# Revit family: Faucet-Wall_Mount_Utility-KALLISTA-Kallista_Foundations-P31570
name_source: partatom
category: Plumbing Fixtures
units: mm (PartAtom-declared; Revit-internal decimal feet)

## family parameters
Cut with Voids When Loaded = No
Host = Face
OmniClass Number = 23.31.11.00
Part Type = Normal
Room Calculation Point = No
Round Connector Dimension = Use Diameter
Shared = No

## types (6) — shared parameters
ADA Compliant = No
Assembly Code = D2010
CW Connection = Yes
Cold Water Inlet = Cold Water Inlet
Date Modified = 03/06/2024
Default Elevation = 36"
Description = Traditional Wall Mount Pot Filler
Drain Included = No
Flow Rate = 3 GPM
HW Connection = Yes
Handle Clearance 1 = 2 5/16"
Handle Clearance 2 = 2 5/16"
Height = 5 1/4"
Hot Water Inlet = Hot Water Inlet
L1 = 13 1/8"
L2 = 8 7/8"
Length = 22"
Manufacturer = Kallista Co.
Master Format 2014 = 22 41 39
Master Format 2014 Name = Residential Faucets, Supplies, and Trim
Material = Premium Metal Construction
Pressure = 60.00 psi
Product Name = Kallista Foundations
Spout Reach = 4 1/4"
URL = https://www.kallista.com
Vent Connection = No
Waste Connection = No
Waste Water Outlet = Waste Water Outlet
WaterSense Certified = No
Width = 2 3/4"

## per-type parameters (varying)
| type | Finish | Model | Type |
| AD-Nickel Silver | Kallista-Metal-AD-Nickel_Silver | P31570-00-AD | 1 |
| AG-Brushed Nickel | Kallista-Metal-AG-Brushed_Nickel | P31570-00-AG | 2 |
| CP-Chrome | Kallista-Metal-CP-Chrome | P31570-00-CP | 3 |
| ULB-Unlaquered Brass | Kallista-Metal-ULB-Unlaquered_Brass | P31570-00-ULB | 4 |
| SN-Polished Nickel | Kallista-Metal-SN-Polished_Nickel | P31570-00-SN | 5 |
| VS-Stainless | Kallista-Metal-VS-Stainless | P31570-00-VS | 6 |

## geometry (parser evidence)
native form markers: Sweep x5
no freeform markers — native parametric forms only
